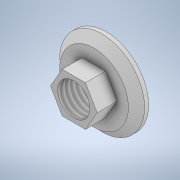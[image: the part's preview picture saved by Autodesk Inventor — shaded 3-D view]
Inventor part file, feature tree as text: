
AUTODESK INVENTOR PART (.ipt)
format: ipt  version: 2021 (Build 250183000, 183)  size: 126,464 bytes
history: native  units: in
note: dims shown in document units (in); Inventor stores cm internally (conversion verified against a paired STEP export)
features: other x2, thread x1
ambient origin geometry x8: Origin, YZ Plane, XZ Plane, XY Plane, X Axis, Y Axis, Z Axis, Center Point
bodies: Body1 (feature_tree)
feature tree (3):
  other  "Sólido2"
  thread  "Rosca1"  [1 undecoded]
  other  "Sólido1"
note: 1 required parameter value undecoded (feature->parameter linkage not recoverable at this tier; creation-order binding heuristic only, values carry confidence <= 0.55)
